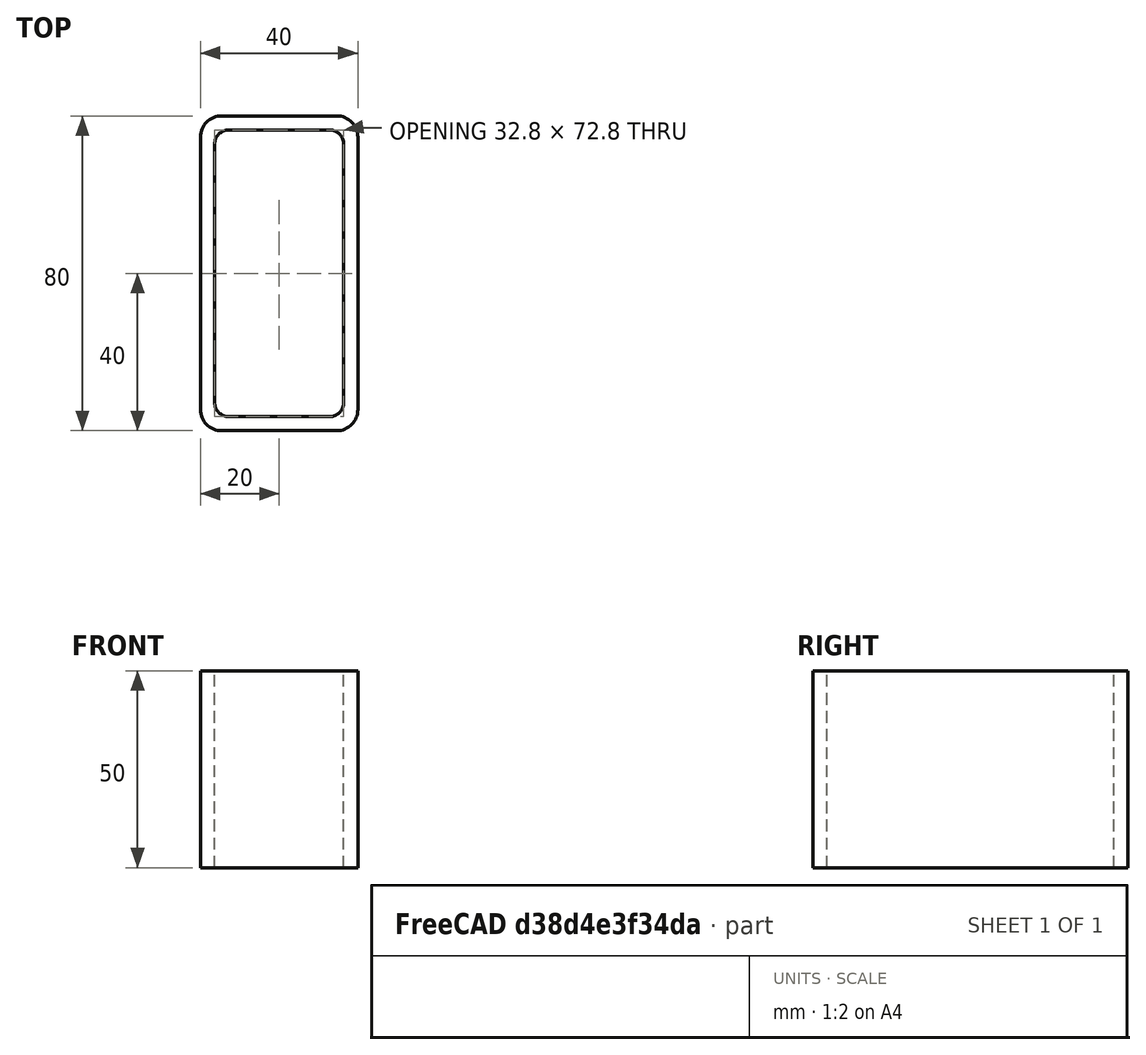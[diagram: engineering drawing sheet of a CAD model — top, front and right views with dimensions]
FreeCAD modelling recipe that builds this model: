
FCSTD DOCUMENT  (FreeCAD 0.15R4671 (Git))
Label: Rectangular hollow section 80x40x3.6 EN10219 S235JRH
License: All rights reserved
LicenseURL: http://en.wikipedia.org/wiki/All_rights_reserved
objects: Sketcher::SketchObject×1, Part::Extrusion×1
note: 2 computed .brp shape members not serialized (recipe doc carries the construction recipe); baked Part::Feature solids carry a one-line shape summary decoded from their .brp

FEATURE [Sketcher::SketchObject] Sketch
  sketch-geometry (16):
    g0: LineSegment StartX=-12.8 StartY=36.4 StartZ=0 EndX=12.8 EndY=36.4 EndZ=0
    g1: LineSegment StartX=16.4 StartY=32.8 StartZ=0 EndX=16.4 EndY=-32.8 EndZ=0
    g2: LineSegment StartX=12.8 StartY=-36.4 StartZ=0 EndX=-12.8 EndY=-36.4 EndZ=0
    g3: LineSegment StartX=-16.4 StartY=-32.8 StartZ=0 EndX=-16.4 EndY=32.8 EndZ=0
    g4: LineSegment StartX=-14.6 StartY=40 StartZ=0 EndX=14.6 EndY=40 EndZ=0
    g5: LineSegment StartX=20 StartY=34.6 StartZ=0 EndX=20 EndY=-34.6 EndZ=0
    g6: LineSegment StartX=14.6 StartY=-40 StartZ=0 EndX=-14.6 EndY=-40 EndZ=0
    g7: LineSegment StartX=-20 StartY=-34.6 StartZ=0 EndX=-20 EndY=34.6 EndZ=0
    g8: ArcOfCircle CenterX=-12.8 CenterY=32.8 CenterZ=0 NormalX=0 NormalY=0 NormalZ=1 Radius=3.6 StartAngle=1.5708 EndAngle=3.14159
    g9: ArcOfCircle CenterX=12.8 CenterY=32.8 CenterZ=0 NormalX=0 NormalY=0 NormalZ=1 Radius=3.6 StartAngle=0 EndAngle=1.5708
    g10: ArcOfCircle CenterX=12.8 CenterY=-32.8 CenterZ=0 NormalX=0 NormalY=0 NormalZ=1 Radius=3.6 StartAngle=4.71239 EndAngle=6.28319
    g11: ArcOfCircle CenterX=-12.8 CenterY=-32.8 CenterZ=0 NormalX=0 NormalY=0 NormalZ=1 Radius=3.6 StartAngle=3.14159 EndAngle=4.71239
    g12: ArcOfCircle CenterX=14.6 CenterY=34.6 CenterZ=0 NormalX=0 NormalY=0 NormalZ=1 Radius=5.4 StartAngle=0 EndAngle=1.5708
    g13: ArcOfCircle CenterX=14.6 CenterY=-34.6 CenterZ=0 NormalX=0 NormalY=0 NormalZ=1 Radius=5.4 StartAngle=4.71239 EndAngle=6.28319
    g14: ArcOfCircle CenterX=-14.6 CenterY=-34.6 CenterZ=0 NormalX=0 NormalY=0 NormalZ=1 Radius=5.4 StartAngle=3.14159 EndAngle=4.71239
    g15: ArcOfCircle CenterX=-14.6 CenterY=34.6 CenterZ=0 NormalX=0 NormalY=0 NormalZ=1 Radius=5.4 StartAngle=1.5708 EndAngle=3.14159
  constraints (36):
    c: Horizontal(g2)
    c: Vertical(g3)
    c: Horizontal(g6)
    c: Vertical(g7)
    c: Tangent(g3,g8) = 1.5708
    c: Tangent(g0,g8) = 1.5708
    c: Tangent(g0,g9) = 1.5708
    c: Tangent(g1,g9) = 1.5708
    c: Tangent(g1,g10) = 1.5708
    c: Tangent(g2,g10) = 1.5708
    c: Tangent(g2,g11) = 1.5708
    c: Tangent(g3,g11) = 1.5708
    c: Tangent(g4,g12) = 1.5708
    c: Tangent(g5,g12) = 1.5708
    c: Tangent(g5,g13) = 1.5708
    c: Tangent(g6,g13) = 1.5708
    c: Tangent(g6,g14) = 1.5708
    c: Tangent(g7,g14) = 1.5708
    c: Tangent(g7,g15) = 1.5708
    c: Tangent(g4,g15) = 1.5708
    c: Equal(g9,g8)
    c: Equal(g9,g11)
    c: Equal(g9,g10)
    c: Equal(g12,g15)
    c: Equal(g12,g14)
    c: Equal(g12,g13)
    c: Symmetric(g4,g6,g-1)
    c: Symmetric(g7,g5,g-2)
    c: DistanceY(g4,g6) = -80
    c: DistanceX(g7,g5) = 40
    c: Symmetric(g3,g1,g-2)
    c: Symmetric(g0,g2,g-1)
    c: DistanceY(g0,g4) = 3.6
    c: DistanceX(g5,g1) = -3.6
    c: Radius(g9) = 3.6
    c: Radius(g12) = 5.4
FEATURE [Part::Extrusion] Extrude  label="Rectangular hollow section 80x40x3.6 EN10219 S235JRH"
  Base = -> Sketch
  Dir = (0,0,50)
  Solid = true
